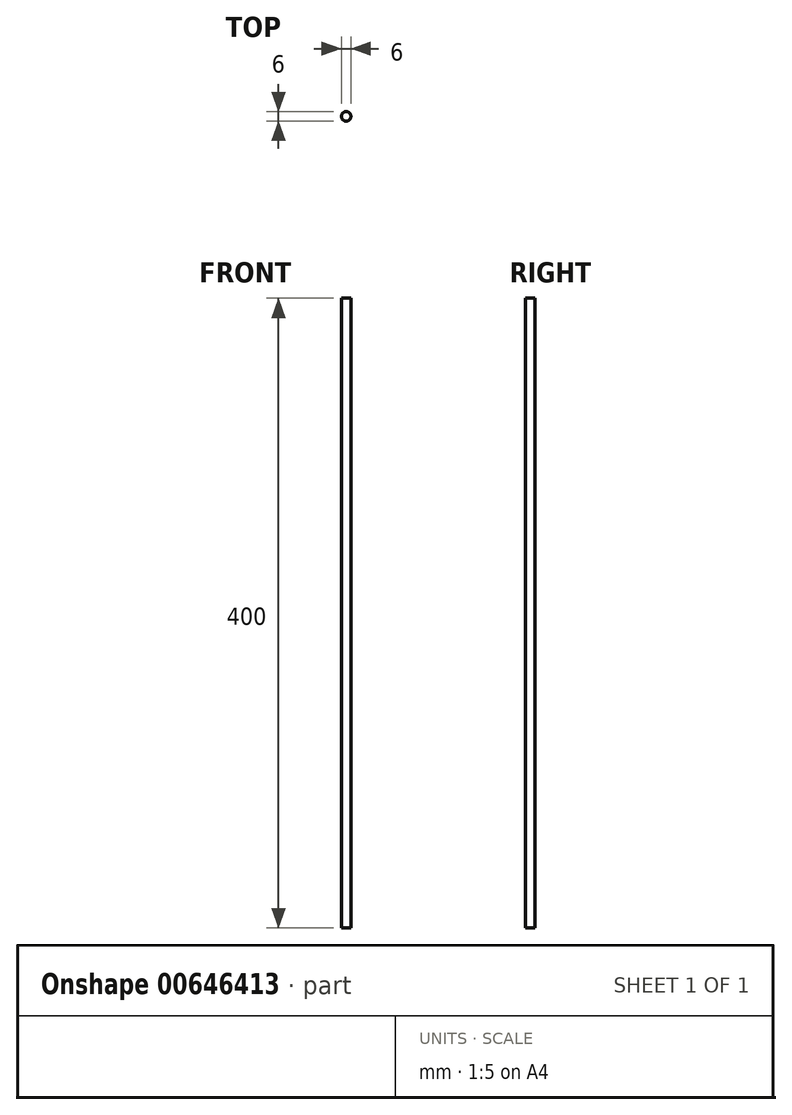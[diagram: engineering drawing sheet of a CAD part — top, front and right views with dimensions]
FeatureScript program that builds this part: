
annotation { "Feature Type Name" : "Feature", "Feature Type Description" : "" }
export const myFeature = defineFeature(function(context is Context, id is Id, definition is map)
    precondition{}
    {
        {
            var Q0;
            Q0=qCreatedBy(makeId("Top.planeOp"),FACE);
            var sketch = newSketch(context, id + "F0", { "sketchPlane" : qUnion([Q0])});
            skCircle(sketch, "E0", {"center": v(0, 0) * mm, "radius": 3 * mm});
            skSolve(sketch);
        }
        {
            var Q0;
            Q0 = qSketchRegion(id + "F0", true);
            extrude(context, id + "F1", {"entities" : qUnion([Q0]), "depth" : 400 * mm, "offsetDistance" : 25 * mm});
        }
    });
